# Revit family: 3-672-xx - 37-672-xx - Luna (Pendant)
name_source: partatom
category: Lighting Fixtures
revit_build: Autodesk Revit 2018 (Build: 20180423_1000(x64)
units: mm (PartAtom-declared; Revit-internal decimal feet)

## family parameters
Always vertical = Yes
Cut with Voids When Loaded = No
Host = Ceiling
Light Source = Yes
OmniClass Number = 23.80.70.11
OmniClass Title = Luminaries for Internal Lighting
Part Type = Normal
Room Calculation Point = No
Round Connector Dimension = Use Diameter
Shared = No

## types (4) — shared parameters
Braided Cord = Braided Cord
Color Filter = 16777215
Diffuser = Oxygen Lighting - Diffuser - White Opal Glass
Dimming Lamp Color Temperature Shift = <None>
Keynote = LED array lamp
Lamp = LED Array
Manufacturer = Oxygen Lighting
Model = 3-672-xx / 37-672-xx
Photometric Web File = 3-672-24 Luna Pendant.ies
References = 3=120 V / 37= 277 V
Tilt Angle = 90.00°
URL = http://www.oxygenlighting.com
Wattage Comments = 10.42 W at 120 V

## per-type parameters (varying)
| type | Metal finish |
| 3-672-40 / 37-672-40 - Luna | Oxygen Lighting - Metal Finish - 40 - Aged Brass |
| 3-672-20 / 37-672-20 - Luna | Oxygen Lighting - Metal Finish - 20 - Polished Nickel |
| 3-672-22 / 37-672-22 - Luna | Oxygen Lighting - Metal Finish - 22 - Oiled Bronze |
| 3-672-24 / 37-672-24 - Luna | Oxygen Lighting - Metal Finish - 24 - Satin Nickel |

## geometry (parser evidence)
native form markers: Sweep x5
no freeform markers — native parametric forms only
